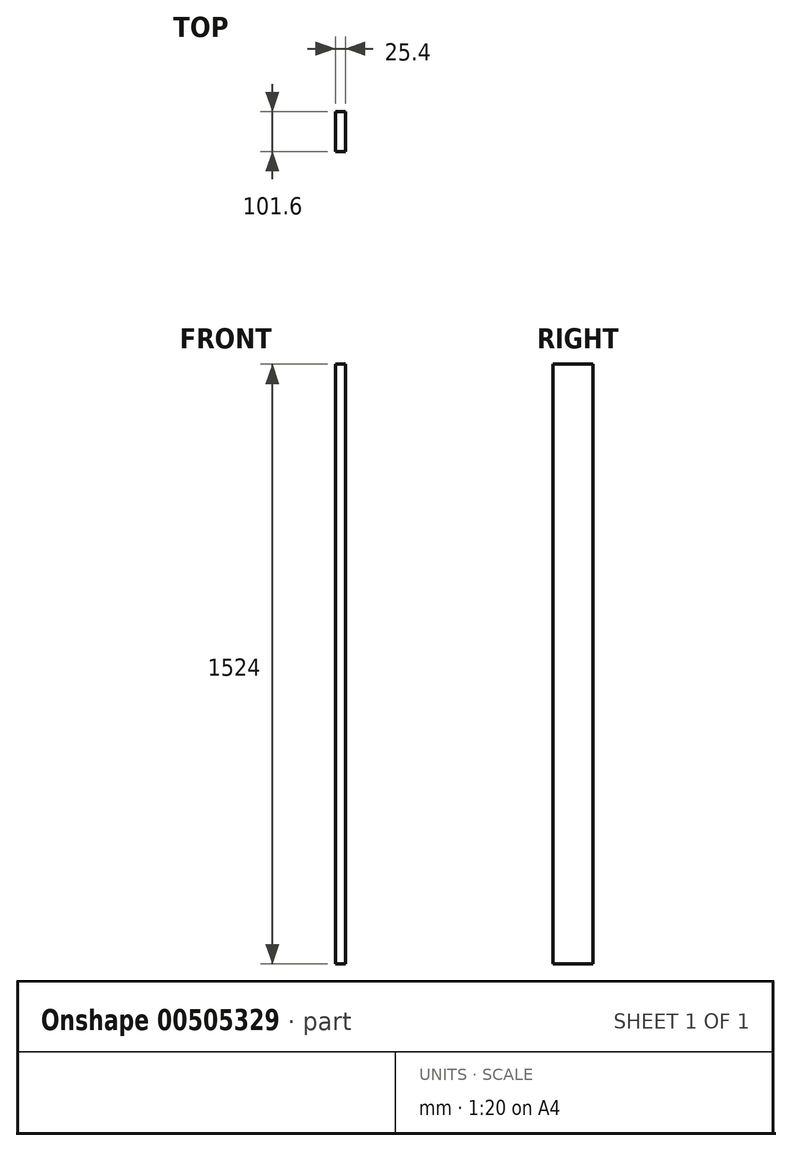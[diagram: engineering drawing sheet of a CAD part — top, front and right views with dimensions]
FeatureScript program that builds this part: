
annotation { "Feature Type Name" : "Feature", "Feature Type Description" : "" }
export const myFeature = defineFeature(function(context is Context, id is Id, definition is map)
    precondition{}
    {
        {
            var Q0;
            Q0=qCreatedBy(makeId("Top.planeOp"),FACE);
            var sketch = newSketch(context, id + "F0", { "sketchPlane" : qUnion([Q0])});
            skLineSegment(sketch, "E0.bottom", {"start": v(25.4, 101.6) * mm, "end": v(0, 101.6) * mm});
            skLineSegment(sketch, "E0.top", {"start": v(25.4, 0) * mm, "end": v(0, 0) * mm});
            skLineSegment(sketch, "E0.left", {"start": v(25.4, 101.6) * mm, "end": v(25.4, 0) * mm});
            skLineSegment(sketch, "E0.right", {"start": v(0, 101.6) * mm, "end": v(0, 0) * mm});
            skSolve(sketch);
        }
        {
            var Q0;
            Q0 = qSketchRegion(id + "F0", true);
            extrude(context, id + "F1", {"entities" : qUnion([Q0]), "depth" : 1524 * mm});
        }
    });
